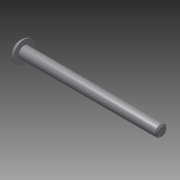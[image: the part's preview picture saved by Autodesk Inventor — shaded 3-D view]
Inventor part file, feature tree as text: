
AUTODESK INVENTOR PART (.ipt)
format: ipt  version: 2015 (Build 190159000, 159)  size: 116,224 bytes
history: native  units: in
note: dims shown in document units (in); Inventor stores cm internally (conversion verified against a paired STEP export)
features: other x3, extrude x1, chamfer x1, imported_body x1, sketch x1
ambient origin geometry x8: Origin, YZ Plane, XZ Plane, XY Plane, X Axis, Y Axis, Z Axis, Center Point
bodies: Body1 (feature_tree)
feature tree (7):
  other  "Bolt 2.0 inch"
  parser-record x1  (decoder bookkeeping rows leaked as tree rows — omitted from the tree; the rows remain in map.json)
  other  "Bolt"
  extrude  "thread length"  Depth=2.0in TaperAngle=0.0deg
  chamfer  "thread chamfer"  Distance=0.02in Angle=45.0deg
  imported_body  "Base1"
  sketch  "Sketch1"  dims[d0=0.164in d1=2.0in d2=0.0in d3=0.02in d4=0.125in d5=45.0deg d7=0.0in d9=0.0in]
